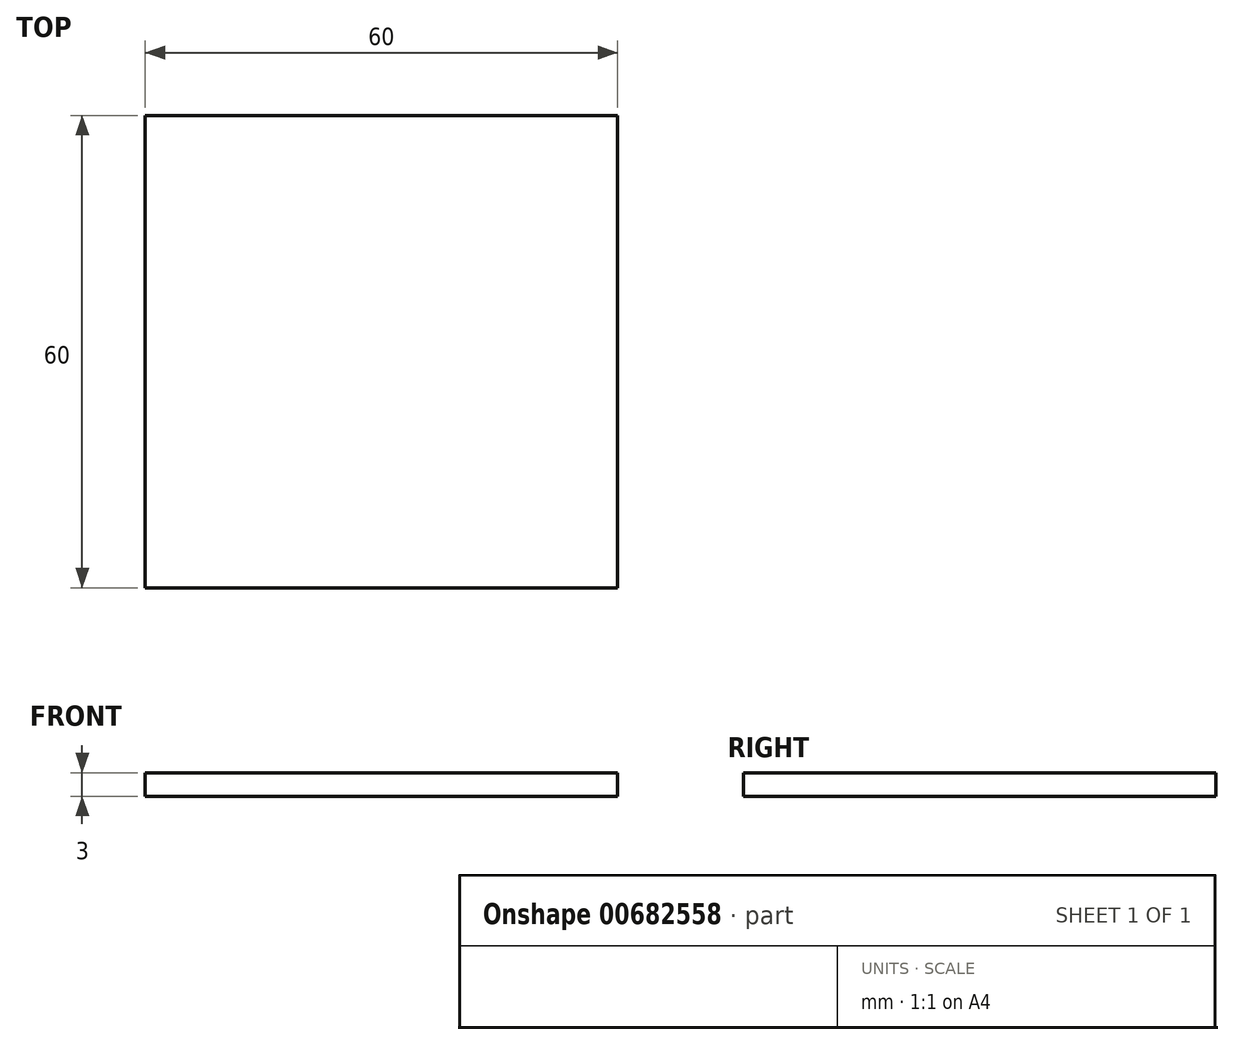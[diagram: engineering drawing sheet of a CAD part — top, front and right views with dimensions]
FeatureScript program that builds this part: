
annotation { "Feature Type Name" : "Feature", "Feature Type Description" : "" }
export const myFeature = defineFeature(function(context is Context, id is Id, definition is map)
    precondition{}
    {
        {
            var Q0;
            Q0=qCreatedBy(makeId("Top.planeOp"),FACE);
            var sketch = newSketch(context, id + "F0", { "sketchPlane" : qUnion([Q0])});
            skLineSegment(sketch, "E0.bottom", {"start": v(0, 0) * mm, "end": v(60, 0) * mm});
            skLineSegment(sketch, "E0.top", {"start": v(0, -60) * mm, "end": v(60, -60) * mm});
            skLineSegment(sketch, "E0.left", {"start": v(0, 0) * mm, "end": v(0, -60) * mm});
            skLineSegment(sketch, "E0.right", {"start": v(60, 0) * mm, "end": v(60, -60) * mm});
            skPoint(sketch, "E1.oppositeSnap0", {"position": v(30, 0) * mm});
            skPoint(sketch, "E1.top.end.orphan", {"position": v(30, 6.91) * mm});
            skSolve(sketch);
        }
        {
            var Q0;
            Q0 = qSketchRegion(id + "F0", true);
            extrude(context, id + "F1", {"entities" : qUnion([Q0]), "depth" : 3 * mm, "offsetDistance" : 25 * mm});
        }
    });
